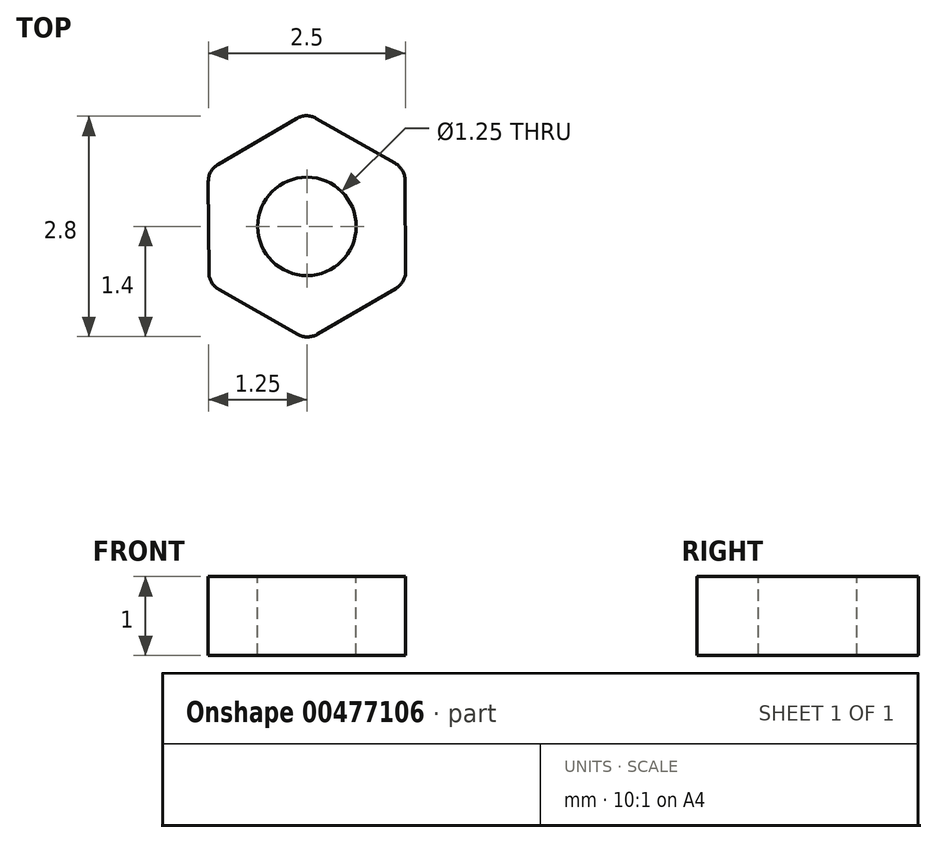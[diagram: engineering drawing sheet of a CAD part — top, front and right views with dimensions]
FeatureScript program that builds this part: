
annotation { "Feature Type Name" : "Feature", "Feature Type Description" : "" }
export const myFeature = defineFeature(function(context is Context, id is Id, definition is map)
    precondition{}
    {
        {
            var Q0;
            Q0=qCreatedBy(makeId("Top.planeOp"),FACE);
            var sketch = newSketch(context, id + "F0", { "sketchPlane" : qUnion([Q0])});
            skCircle(sketch, "E0.cCircle", {"center": v(0, 0) * mm, "radius": 5 * mm, "construction": true});
            skLineSegment(sketch, "E0.0", {"start": v(5.02, -2.85) * mm, "end": v(0.04, -5.77) * mm});
            skLineSegment(sketch, "E0.1", {"start": v(0.04, -5.77) * mm, "end": v(-4.98, -2.92) * mm});
            skLineSegment(sketch, "E0.2", {"start": v(-4.98, -2.92) * mm, "end": v(-5.02, 2.85) * mm});
            skLineSegment(sketch, "E0.3", {"start": v(-5.02, 2.85) * mm, "end": v(-0.04, 5.77) * mm});
            skLineSegment(sketch, "E0.4", {"start": v(-0.04, 5.77) * mm, "end": v(4.98, 2.92) * mm});
            skLineSegment(sketch, "E0.5", {"start": v(4.98, 2.92) * mm, "end": v(5.02, -2.85) * mm});
            skPoint(sketch, "E0.0.midPoint", {"position": v(2.53, -4.31) * mm});
            skSolve(sketch);
        }
        {
            var Q0;
            Q0 = qSketchRegion(id + "F0", true);
            extrude(context, id + "F1", {"entities" : qUnion([Q0]), "depth" : 4 * mm});
        }
        {
            var Q0;
            Q0=makeQuery(id+"F1.opExtrude","CAP_FACE",FACE,{"disambiguationData":[OSD([sQuery(id+"F0.wireOp",EDGE,"E0.0"),sQuery(id+"F0.wireOp",EDGE,"E0.1"),sQuery(id+"F0.wireOp",EDGE,"E0.2"),sQuery(id+"F0.wireOp",EDGE,"E0.3"),sQuery(id+"F0.wireOp",EDGE,"E0.4"),sQuery(id+"F0.wireOp",EDGE,"E0.5")])],"isStart":false});
            var sketch = newSketch(context, id + "F2", { "sketchPlane" : qUnion([Q0])});
            skCircle(sketch, "E1", {"center": v(0, 0) * mm, "radius": 2.5 * mm});
            skSolve(sketch);
        }
        {
            var Q0;
            Q0=sQuery(id+"F2.wireOp",VERTEX,"E1.center");
            var Q1;
            Q1=makeQuery(id+"F1.opExtrude","SWEPT_BODY",BODY,{"disambiguationData":[OSD([sQuery(id+"F0.wireOp",EDGE,"E0.0"),sQuery(id+"F0.wireOp",EDGE,"E0.1"),sQuery(id+"F0.wireOp",EDGE,"E0.2"),sQuery(id+"F0.wireOp",EDGE,"E0.3"),sQuery(id+"F0.wireOp",EDGE,"E0.4"),sQuery(id+"F0.wireOp",EDGE,"E0.5")])]});
            hole(context, id + "F3", {"style" : HoleStyle.SIMPLE, "endStyle" : HoleEndStyle.BLIND, "holeDiameter" : 5 * mm, "holeDepth" : 10 * mm, "isTappedThrough" : true, "tappedDepth" : 12 * mm, "tapClearance" : 3, "locations" : qUnion([Q0]), "scope" : qUnion([Q1])});
        }
        {
            var Q0;
            Q0=makeQuery(id+"F1.opExtrude","SWEPT_EDGE",EDGE,{"disambiguationData":[OSD([sQuery(id+"F0.wireOp",EDGE,"E0.2"),sQuery(id+"F0.wireOp",EDGE,"E0.3")])]});
            var Q1;
            Q1=makeQuery(id+"F1.opExtrude","SWEPT_EDGE",EDGE,{"disambiguationData":[OSD([sQuery(id+"F0.wireOp",EDGE,"E0.3"),sQuery(id+"F0.wireOp",EDGE,"E0.4")])]});
            var Q2;
            Q2=makeQuery(id+"F1.opExtrude","SWEPT_EDGE",EDGE,{"disambiguationData":[OSD([sQuery(id+"F0.wireOp",EDGE,"E0.1"),sQuery(id+"F0.wireOp",EDGE,"E0.2")])]});
            var Q3;
            Q3=makeQuery(id+"F1.opExtrude","SWEPT_EDGE",EDGE,{"disambiguationData":[OSD([sQuery(id+"F0.wireOp",EDGE,"E0.0"),sQuery(id+"F0.wireOp",EDGE,"E0.1")])]});
            var Q4;
            Q4=makeQuery(id+"F1.opExtrude","SWEPT_EDGE",EDGE,{"disambiguationData":[OSD([sQuery(id+"F0.wireOp",EDGE,"E0.0"),sQuery(id+"F0.wireOp",EDGE,"E0.5")])]});
            var Q5;
            Q5=makeQuery(id+"F1.opExtrude","SWEPT_EDGE",EDGE,{"disambiguationData":[OSD([sQuery(id+"F0.wireOp",EDGE,"E0.4"),sQuery(id+"F0.wireOp",EDGE,"E0.5")])]});
            fillet(context, id + "F4", {"entities" : qUnion([Q0, Q1, Q2, Q3, Q4, Q5]), "radius" : 1 * mm, "tangentPropagation" : true, "allowEdgeOverflow" : false});
        }
        {
            var Q0;
            Q0=makeQuery(id+"F1.opExtrude","SWEPT_BODY",BODY,{"disambiguationData":[OSD([sQuery(id+"F0.wireOp",EDGE,"E0.0"),sQuery(id+"F0.wireOp",EDGE,"E0.1"),sQuery(id+"F0.wireOp",EDGE,"E0.2"),sQuery(id+"F0.wireOp",EDGE,"E0.3"),sQuery(id+"F0.wireOp",EDGE,"E0.4"),sQuery(id+"F0.wireOp",EDGE,"E0.5")])]});
            var Q1;
            Q1=qCreatedBy(makeId("Origin.pointOp"),VERTEX);
            transform(context, id + "F5", {"entities" : qUnion([Q0]), "transformType" : TransformType.SCALE_UNIFORMLY, "scale" : .25, "scalePoint" : qUnion([Q1]), "makeCopy" : false});
        }
    });
